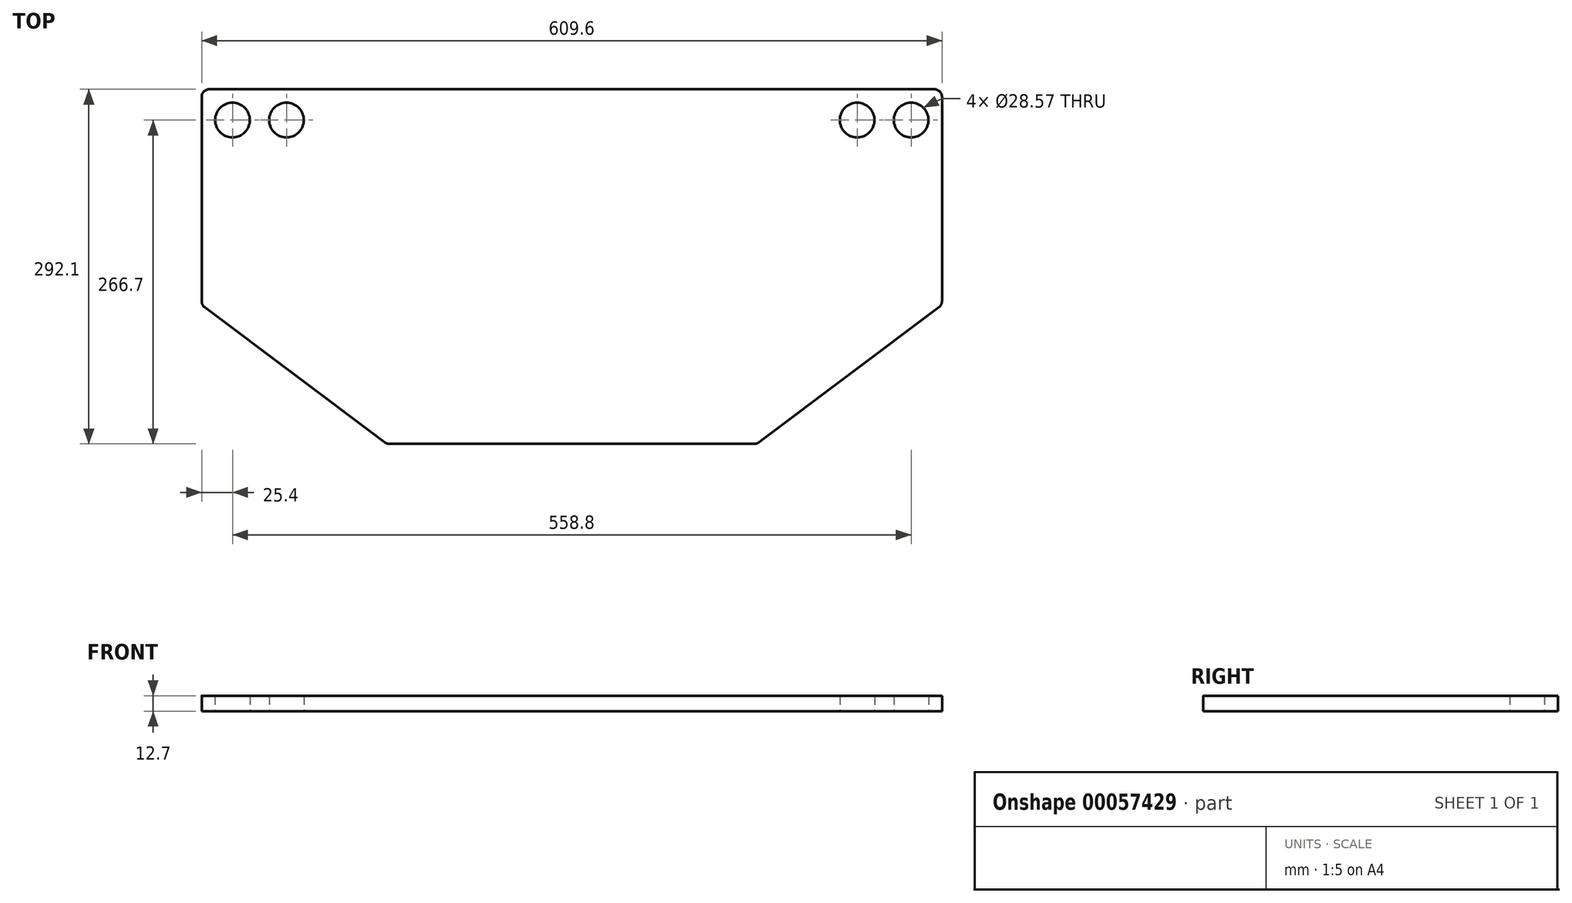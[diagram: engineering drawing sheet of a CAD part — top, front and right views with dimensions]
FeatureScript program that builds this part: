
annotation { "Feature Type Name" : "Feature", "Feature Type Description" : "" }
export const myFeature = defineFeature(function(context is Context, id is Id, definition is map)
    precondition{}
    {
        {
            var Q0;
            Q0=qCreatedBy(makeId("Top.planeOp"),FACE);
            var sketch = newSketch(context, id + "F0", { "sketchPlane" : qUnion([Q0])});
            skLineSegment(sketch, "E0", {"start": v(-304.8, -6.35) * mm, "end": v(-304.8, -174.63) * mm});
            skLineSegment(sketch, "E1", {"start": v(304.8, -6.35) * mm, "end": v(304.8, -174.62) * mm});
            skLineSegment(sketch, "E2", {"start": v(-298.45, 0) * mm, "end": v(298.45, 0) * mm});
            skLineSegment(sketch, "E3", {"start": v(-150.28, -292.1) * mm, "end": v(150.28, -292.1) * mm});
            skLineSegment(sketch, "E4", {"start": v(154.1, -290.83) * mm, "end": v(302.26, -179.7) * mm});
            skLineSegment(sketch, "E5", {"start": v(-302.26, -179.7) * mm, "end": v(-154.1, -290.83) * mm});
            skCircle(sketch, "E6", {"center": v(-279.4, -25.4) * mm, "radius": 14.29 * mm});
            skCircle(sketch, "E7", {"center": v(-234.95, -25.4) * mm, "radius": 14.29 * mm});
            skCircle(sketch, "E8", {"center": v(279.4, -25.4) * mm, "radius": 14.29 * mm});
            skCircle(sketch, "E9", {"center": v(234.95, -25.4) * mm, "radius": 14.29 * mm});
            skPoint(sketch, "E10.visualSharp", {"position": v(-304.8, 0) * mm});
            skArc(sketch, "E10.filletArc", {"start": v(-298.45, 0) * mm, "mid": v(-302.94, -1.86) * mm, "end": v(-304.8, -6.35) * mm});
            skPoint(sketch, "E11.visualSharp", {"position": v(-304.8, -177.8) * mm});
            skArc(sketch, "E11.filletArc", {"start": v(-304.8, -174.63) * mm, "mid": v(-304.13, -177.46) * mm, "end": v(-302.26, -179.7) * mm});
            skPoint(sketch, "E12.visualSharp", {"position": v(-152.4, -292.1) * mm});
            skArc(sketch, "E12.filletArc", {"start": v(-154.1, -290.83) * mm, "mid": v(-152.3, -291.77) * mm, "end": v(-150.28, -292.1) * mm});
            skPoint(sketch, "E13.visualSharp", {"position": v(152.4, -292.1) * mm});
            skArc(sketch, "E13.filletArc", {"start": v(150.28, -292.1) * mm, "mid": v(152.3, -291.77) * mm, "end": v(154.1, -290.83) * mm});
            skPoint(sketch, "E14.visualSharp", {"position": v(304.8, -177.8) * mm});
            skArc(sketch, "E14.filletArc", {"start": v(302.26, -179.7) * mm, "mid": v(304.13, -177.46) * mm, "end": v(304.8, -174.62) * mm});
            skPoint(sketch, "E15.visualSharp", {"position": v(304.8, 0) * mm});
            skArc(sketch, "E15.filletArc", {"start": v(304.8, -6.35) * mm, "mid": v(302.94, -1.86) * mm, "end": v(298.45, 0) * mm});
            skSolve(sketch);
        }
        {
            var Q0;
            Q0 = qSketchRegion(id + "F0", true);
            extrude(context, id + "F1", {"entities" : qUnion([Q0]), "depth" : 12.7 * mm});
        }
    });
